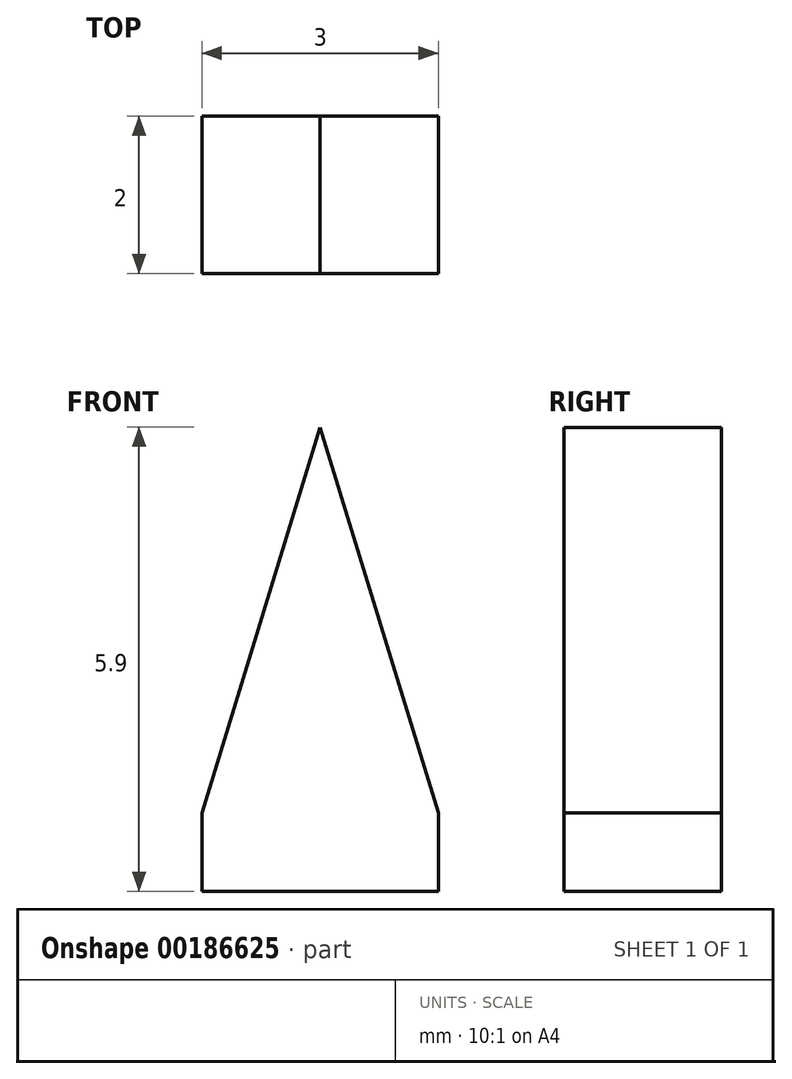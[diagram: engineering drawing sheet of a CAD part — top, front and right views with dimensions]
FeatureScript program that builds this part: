
annotation { "Feature Type Name" : "Feature", "Feature Type Description" : "" }
export const myFeature = defineFeature(function(context is Context, id is Id, definition is map)
    precondition{}
    {
        {
            var Q0;
            Q0=qCreatedBy(makeId("Front.planeOp"),FACE);
            var sketch = newSketch(context, id + "F0", { "sketchPlane" : qUnion([Q0])});
            skLineSegment(sketch, "E0.bottom", {"start": v(1.5, -0.5) * mm, "end": v(-1.5, -0.5) * mm});
            skLineSegment(sketch, "E0.top", {"start": v(1.5, 0.5) * mm, "end": v(-1.5, 0.5) * mm});
            skLineSegment(sketch, "E0.left", {"start": v(1.5, -0.5) * mm, "end": v(1.5, 0.5) * mm});
            skLineSegment(sketch, "E0.right", {"start": v(-1.5, -0.5) * mm, "end": v(-1.5, 0.5) * mm});
            skPoint(sketch, "E0.middle", {"position": v(0, 0) * mm});
            skCircle(sketch, "E1.cCircle", {"center": v(0, 1.37) * mm, "radius": 1.18 * mm, "construction": true});
            skLineSegment(sketch, "E1.0", {"start": v(0, 5.4) * mm, "end": v(1.5, 0.5) * mm});
            skLineSegment(sketch, "E1.2", {"start": v(-1.5, 0.5) * mm, "end": v(0, 5.4) * mm});
            skPoint(sketch, "E1.0.midPoint", {"position": v(0.86, 2.17) * mm});
            skSolve(sketch);
        }
        {
            var Q0;
            Q0 = qSketchRegion(id + "F0", true);
            extrude(context, id + "F1", {"entities" : qUnion([Q0]), "oppositeDirection" : true, "depth" : 2 * mm});
        }
    });
